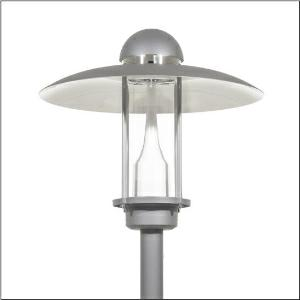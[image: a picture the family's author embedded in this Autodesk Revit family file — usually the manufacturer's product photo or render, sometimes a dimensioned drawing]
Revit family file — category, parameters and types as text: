
# Revit family: city-light_elegance_iq___st1_2a_5xa5265af14h_1cc4
name_source: partatom
category: Lighting Fixtures
units: mm (PartAtom-declared; Revit-internal decimal feet)

## family parameters
Cut with Voids When Loaded = No
Host = Face
Light Source = No
Part Type = Normal
Room Calculation Point = No
Round Connector Dimension = Use Diameter
Shared = No

## types (1)
- --- (1 x LED, 1470 lm, 12.9 W, 2200K)
    Apparent Load = 13 VA
    CIE Flux Codes = 22 62 94 98 100
    Color Rendering = 70
    Color Temperature = 2200K
    Default Elevation = 1800 mm
    Description = City-Light Elegance iQ, mast luminaire, Module 540 iQ-SR, primary light control with 3 zone facetted reflector, of plastic, silver coated, highly specular, structured, primary optical cover: cover, of PMMA, transparent, light distribution: ST1.2a, light emission: direct distribution, primary light characteristic: asymmetric, installation type: post-top, LED, High Power LED, rated luminous flux: 1.470lm, luminous efficacy: 114lm/W, light colour: 722, colour temperature: 2200K, control gear: ECG iQ, control: presetting dimming logarithmic, Street-Remote, Auto-Match, Temp-Guard, Lumen-Switch, Night-Set, Smart-Wire, Light-Fading, Desk-Remote (wireless, voltage-free reading and setting of iQ features in the workshop via application-optimized NFC function/RFID function), optimised constant luminous flux control (CLO 2.0), with terminal, 6-pole, max. 2.5mm², mains connection: 230..240V, AC, 50/60Hz, start of lifetime: 13W, end of service life: 13W, reduction: 6W, luminaire housing, upper part, of aluminium, coated, Siteco® metallic grey (DB 702S), diameter: 750mm, height: 675mm, spigot size: d x l = 76 x 70mm (post-top) | with reducer (optional accessory) 60 x 70mm, post-top mast mounting element, of diecast aluminium, coated, Siteco® metallic grey (DB 702S), Module 540 iQ-SR, traffic white (RAL 9016), equipment: standard, protection rating (complete): IP65, insulation class (complete): insulation class II (safety insulation), certification: CE, ENEC, VDE, packaging unit: 1 piece

Light Distribution: ST1.2a
    Height = 675 mm
    Lamp = 1 x LED
    Lamp Light Flux = 1470 lm
    Lamp Power = 12.9 W
    Lamp count = 1
    Length = 750 mm
    Luminous efficacy = 114 lm/W
    Manufacturer = Siteco
    ModVariant = No
    Model = 5XA5265AF14H
    Number of Poles = 1
    OnlyDefault = Yes
    Power Factor = 1
    Product Name = City-Light Elegance iQ | ST1.2a
    Product group = mast luminaire | pylon top
    ProductGroupID = 6100
    Protection Class = Protection class II
    Protection Degree = IP 65
    RLX_Detail_Level = 1
    RLX_Emergency_Light_Flux = 0 lm
    RLX_Emergency_Type = 0
    RLX_Emergency_Type_DB = No
    RlxData = <blob elided: 100333 chars, md5=8d782506>
    Socket = socket
    Standby Power = 0 W
    System Light Flux = 1470 lm
    System Power = 13 W
    Type Comments = factory setting: luminous flux: 100 % | dim-lin: 254 | 516 mA
    Type Image = l_1006912.jpg
    URL = http://relux.com
    VarID = @adj_110063
    Voltage = 0 V
    Weight = 0.00 kg
    Width = 0 mm  [stored 0 ft]

note: [stored X ft] marks values corroborated as IEEE doubles in the binary element streams (Revit-internal decimal feet)

## geometry (parser evidence)
native form markers: Blend x4, Sweep x10
no freeform markers — native parametric forms only
